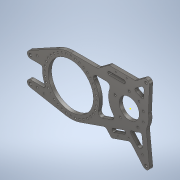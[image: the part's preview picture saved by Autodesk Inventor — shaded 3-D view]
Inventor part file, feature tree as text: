
AUTODESK INVENTOR PART (.ipt)
format: ipt  version: 2021 (Build 250183000, 183)  size: 586,240 bytes
history: native  units: in
note: dims shown in document units (in); Inventor stores cm internally (conversion verified against a paired STEP export)
features: sketch x22, extrude x17, hole x5, fillet x4, chamfer x1, projected_geometry x1
ambient origin geometry x8: Origin, YZ Plane, XZ Plane, XY Plane, X Axis, Y Axis, Z Axis, Center Point
bodies: Body1 (feature_tree)
feature tree (50):
  extrude  "Extrusion13"  Depth=0.5in TaperAngle=0.0deg
  hole  "Hole4"  [1 undecoded]
  extrude  "Extrusion15"  Depth=1.0in
  extrude  "Extrusion16"  Depth=0.5in TaperAngle=0.0deg
  hole  "Hole6"  [1 undecoded]
  extrude  "Extrusion17"  Depth=1.0in
  hole  "Hole7"  [1 undecoded]
  hole  "Hole9"  [1 undecoded]
  hole  "Hole10"  [1 undecoded]
  extrude  "Extrusion18"  Depth=1.0in
  extrude  "Extrusion19"  Depth=0.239in
  sketch  "Sketch33"  dims[d183=0.257in d184=0.75in d185=0.438in d186=0.25in d187=0.5635in d188=1.0in d189=0.8108in d191=1.0in]
  extrude  "Extrusion21"  Depth=0.5in
  extrude  "Extrusion22"  Depth=1.0in
  extrude  "Extrusion23"  Depth=0.75in
  extrude  "Extrusion24"  Depth=0.75in
  fillet  "Fillet2"  Radius=0.25in
  extrude  "Extrusion25"  Depth=1.0in TaperAngle=0.0deg
  extrude  "Extrusion26"  Depth=1.0in TaperAngle=0.0deg
  fillet  "Fillet3"  Radius=0.75in
  extrude  "Extrusion27"  Depth=0.75in
  chamfer  "Chamfer1"  Distance=1.0in
  sketch  "Sketch40"  dims[d211=0.75in d212=0.75in d213=0.25in]
  extrude  "Extrusion29"  Depth=0.25in
  extrude  "Extrusion30"  Depth=1.0in TaperAngle=0.0deg
  fillet  "Fillet4"  Radius=0.75in
  fillet  "Fillet5"  Radius=1.0in
  extrude  "Extrusion32"  Depth=1.0in TaperAngle=0.0deg
  extrude  "Extrusion33"  Depth=0.25in
  sketch  "Sketch14"  dims[d96=8.5in d97=2.16in d98=9.0in d99=5.5in d100=1.0in d101=1.0in d102=6.0in d103=6.0in d104=3.718in d105=1.0in d108=10.718in d109=1.5in d111=0.5in d112=0.0in]
  sketch  "Sketch15"  dims[d113=0.386in d114=0.75in d115=0.762in d116=0.25in d117=0.5635in d118=0.484in d119=0.8108in d132=5.0in]
  sketch  "Sketch18"  dims[d133=17.223in d134=1.0in]
  sketch  "Sketch19"  dims[d135=1.0in d136=0.5in d137=0.0in]
  sketch  "Sketch20"  dims[d138=1.0in d140=4.0in]
  sketch  "Sketch21"  dims[d141=0.5in d142=0.0in d143=1.0in]
  sketch  "Sketch23"  dims[d144=1.625in]
  sketch  "Sketch27"  dims[d145=0.177in d146=0.75in d147=0.332in d148=0.25in d149=0.5635in d150=0.484in d151=0.8108in d155=1.0in d156=0.0in]
  sketch  "Sketch29"  dims[d157=1.625in]
  sketch  "Sketch31"  dims[d159=0.177in d160=0.75in d161=0.332in d162=0.25in d163=0.5635in d164=1.0in d165=0.8108in d178=7.75in]
  sketch  "Sketch32"  dims[d179=3.5433in d181=360.0deg]
  sketch  "Sketch34"  dims[d192=0.0481in d193=1.0in]
  sketch  "Sketch35"  dims[d194=0.3526in d197=0.239in]
  sketch  "Sketch36"  dims[d198=0.1195in d199=0.5in]
  sketch  "Sketch38"  dims[d200=0.266in d201=0.75in d202=0.507in d203=0.25in d204=0.5635in d205=1.0in d206=0.8108in d207=0.1718in]
  sketch  "Sketch39"  dims[d208=15.0deg d210=0.75in]
  sketch  "Sketch42"  dims[d214=0.5in d215=1.0in d216=0.0in]
  sketch  "Sketch43"  dims[d217=0.25in d218=1.0in d219=0.0in d220=0.75in]
  sketch  "Sketch45"  dims[d221=0.5in d223=0.75in]
  sketch  "Sketch46"  dims[d231=0.25in d232=1.0in d233=0.0in d234=0.25in d235=1.0in d236=0.0in d237=0.75in d238=1.0in d239=0.0in d242=1.0in d243=0.0in d244=0.25in d247=0.75in d249=0.75in d250=0.5in d251=2.8in d252=0.375in d253=1.25in d255=0.75in d256=0.75in d257=1.0in d258=0.0in d259=0.25in d260=1.0in d261=0.0in d262=0.25in d263=0.5in d264=1.0in d265=0.0in d266=0.0156in d267=0.125in d268=45.0deg d284=1.0in d285=0.0in d296=6.75in d297=1.0in d298=0.0in d303=3.005in d304=8.715in d305=6.5in d306=0.5in d307=0.5in d308=4.44in d309=0.325in d310=1.9685in d312=360.0deg d314=1.0in d315=0.0in d317=0.061in d318=0.25in d319=0.25in d320=12.85in d321=4.5in d322=1.0in d323=0.0in d324=0.25in d283=0.5in d286=0.0344in]
  projected_geometry  "Project Cut Edges1"
note: 5 required parameter values undecoded (feature->parameter linkage not recoverable at this tier; creation-order binding heuristic only, values carry confidence <= 0.55)
